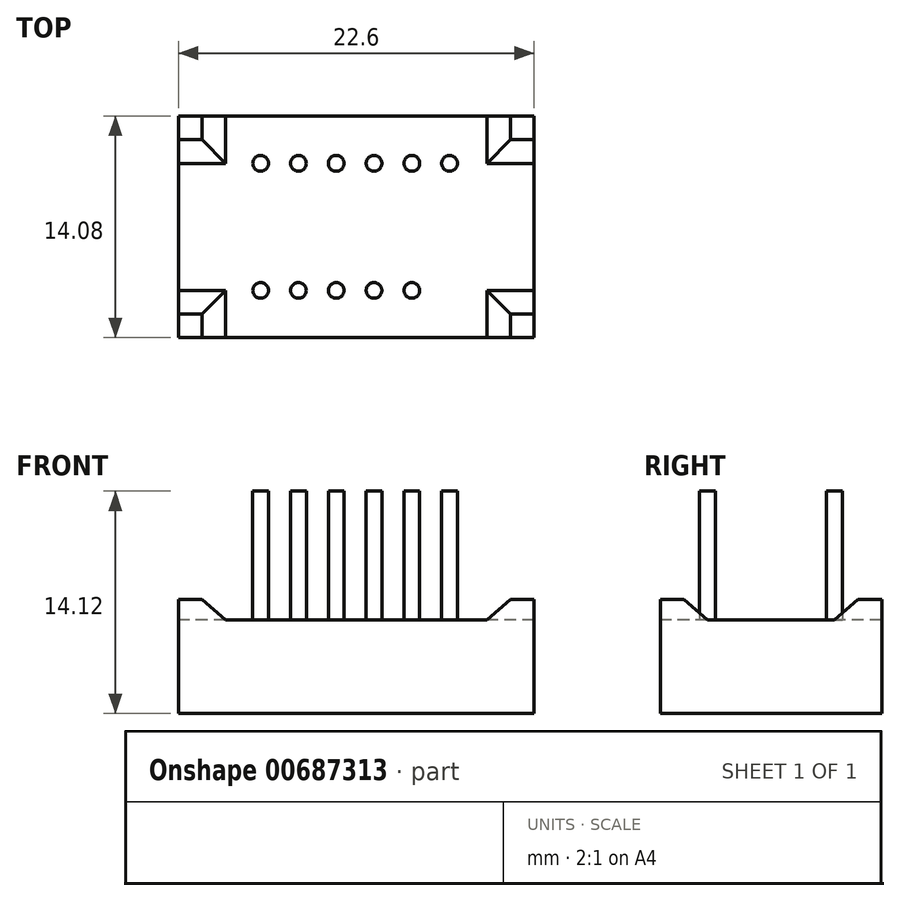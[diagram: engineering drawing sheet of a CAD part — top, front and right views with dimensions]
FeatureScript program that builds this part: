
annotation { "Feature Type Name" : "Feature", "Feature Type Description" : "" }
export const myFeature = defineFeature(function(context is Context, id is Id, definition is map)
    precondition{}
    {
        {
            var Q0;
            Q0=qCreatedBy(makeId("Top.planeOp"),FACE);
            var sketch = newSketch(context, id + "F0", { "sketchPlane" : qUnion([Q0])});
            skLineSegment(sketch, "E0.bottom", {"start": v(11.3, -7.03) * mm, "end": v(-11.3, -7.04) * mm});
            skLineSegment(sketch, "E0.top", {"start": v(11.3, 7.04) * mm, "end": v(-11.3, 7.03) * mm});
            skLineSegment(sketch, "E0.left", {"start": v(11.3, -7.04) * mm, "end": v(11.3, 7.04) * mm});
            skLineSegment(sketch, "E0.right", {"start": v(-11.3, -7.04) * mm, "end": v(-11.3, 7.04) * mm});
            skPoint(sketch, "E0.middle", {"position": v(0, 0) * mm});
            skSolve(sketch);
        }
        {
            var Q0;
            Q0 = qSketchRegion(id + "F0", true);
            extrude(context, id + "F1", {"entities" : qUnion([Q0]), "depth" : 7.24 * mm, "offsetDistance" : 25 * mm});
        }
        {
            var Q0;
            Q0=makeQuery(id+"F1.opExtrude","SWEPT_FACE",FACE,{"disambiguationData":[OSD([sQuery(id+"F0.wireOp",EDGE,"E0.bottom")])]});
            var sketch = newSketch(context, id + "F2", { "sketchPlane" : qUnion([Q0])});
            skLineSegment(sketch, "E1", {"start": v(-9.8, 7.24) * mm, "end": v(-8.3, 5.94) * mm});
            skLineSegment(sketch, "E2", {"start": v(-8.3, 5.94) * mm, "end": v(0, 5.94) * mm});
            skLineSegment(sketch, "E3", {"start": v(-9.8, 7.24) * mm, "end": v(0, 7.24) * mm});
            skLineSegment(sketch, "E4", {"start": v(0, 4.37) * mm, "end": v(0, 9.61) * mm, "construction": true});
            skLineSegment(sketch, "E5.MirrorCS", {"start": v(8.3, 5.94) * mm, "end": v(0, 5.94) * mm});
            skLineSegment(sketch, "E6.MirrorCS", {"start": v(9.8, 7.24) * mm, "end": v(0, 7.24) * mm});
            skLineSegment(sketch, "E7.MirrorCS", {"start": v(9.8, 7.24) * mm, "end": v(8.3, 5.94) * mm});
            skSolve(sketch);
        }
        {
            var Q0;
            Q0 = qSketchRegion(id + "F2", true);
            extrude(context, id + "F3", {"entities" : qUnion([Q0]), "operationType" : NewBodyOperationType.REMOVE, "oppositeDirection" : true, "depth" : 25 * mm, "offsetDistance" : 25 * mm});
        }
        {
            var Q0;
            Q0=makeQuery(id+"F1.opExtrude","SWEPT_FACE",FACE,{"disambiguationData":[OSD([sQuery(id+"F0.wireOp",EDGE,"E0.right")])]});
            var sketch = newSketch(context, id + "F4", { "sketchPlane" : qUnion([Q0])});
            skLineSegment(sketch, "E8", {"start": v(0, 10.08) * mm, "end": v(0, -4.13) * mm, "construction": true});
            skLineSegment(sketch, "E9", {"start": v(-5.54, 7.24) * mm, "end": v(-4.04, 5.94) * mm});
            skLineSegment(sketch, "E10", {"start": v(-4.04, 5.94) * mm, "end": v(0, 5.94) * mm});
            skLineSegment(sketch, "E11", {"start": v(-5.54, 7.24) * mm, "end": v(0, 7.24) * mm});
            skLineSegment(sketch, "E12.MirrorCS", {"start": v(5.54, 7.24) * mm, "end": v(0, 7.24) * mm});
            skLineSegment(sketch, "E13.MirrorCS", {"start": v(4.04, 5.94) * mm, "end": v(0, 5.94) * mm});
            skLineSegment(sketch, "E14.MirrorCS", {"start": v(5.54, 7.24) * mm, "end": v(4.04, 5.94) * mm});
            skSolve(sketch);
        }
        {
            var Q0;
            Q0 = qSketchRegion(id + "F4", true);
            extrude(context, id + "F5", {"entities" : qUnion([Q0]), "operationType" : NewBodyOperationType.REMOVE, "oppositeDirection" : true, "depth" : 25 * mm, "offsetDistance" : 25 * mm});
        }
        {
            var Q0;
            Q0=makeQuery(id+"F5.boolean.opBoolean","MERGE",FACE,{"derivedFrom":[makeQuery(id+"F3.boolean.opBoolean","COPY",FACE,{"derivedFrom":makeQuery(id+"F3.opExtrude","SWEPT_FACE",FACE,{"disambiguationData":[OSD([sQuery(id+"F2.wireOp",EDGE,"E2"),sQuery(id+"F2.wireOp",EDGE,"E5.MirrorCS")])]})})],"fromTools":[makeQuery(id+"F5.opExtrude","SWEPT_FACE",FACE,{"disambiguationData":[OSD([sQuery(id+"F4.wireOp",EDGE,"E10"),sQuery(id+"F4.wireOp",EDGE,"E13.MirrorCS")])]})]});
            var sketch = newSketch(context, id + "F6", { "sketchPlane" : qUnion([Q0])});
            skCircle(sketch, "E15", {"center": v(-6.07, -4.04) * mm, "radius": 0.5 * mm});
            skCircle(sketch, "E16", {"center": v(-6.07, 4.03) * mm, "radius": 0.5 * mm});
            skCircle(sketch, "E17.1.0.0", {"center": v(-3.67, 4.03) * mm, "radius": 0.5 * mm});
            skCircle(sketch, "E17.2.0.0", {"center": v(-1.27, 4.03) * mm, "radius": 0.5 * mm});
            skCircle(sketch, "E17.3.0.0", {"center": v(1.13, 4.03) * mm, "radius": 0.5 * mm});
            skCircle(sketch, "E17.4.0.0", {"center": v(3.53, 4.03) * mm, "radius": 0.5 * mm});
            skCircle(sketch, "E17.5.0.0", {"center": v(5.93, 4.03) * mm, "radius": 0.5 * mm});
            skLineSegment(sketch, "E17.direction1", {"start": v(-6.07, 4.03) * mm, "end": v(-3.67, 4.03) * mm, "construction": true});
            skCircle(sketch, "E18.1.0.0", {"center": v(-3.67, -4.04) * mm, "radius": 0.5 * mm});
            skCircle(sketch, "E18.2.0.0", {"center": v(-1.27, -4.04) * mm, "radius": 0.5 * mm});
            skCircle(sketch, "E18.3.0.0", {"center": v(1.13, -4.04) * mm, "radius": 0.5 * mm});
            skCircle(sketch, "E18.4.0.0", {"center": v(3.53, -4.04) * mm, "radius": 0.5 * mm});
            skLineSegment(sketch, "E18.direction1", {"start": v(-6.07, -4.04) * mm, "end": v(-3.67, -4.04) * mm, "construction": true});
            skSolve(sketch);
        }
        {
            var Q0;
            Q0 = qSketchRegion(id + "F6", true);
            extrude(context, id + "F7", {"entities" : qUnion([Q0]), "operationType" : NewBodyOperationType.ADD, "depth" : 8.18 * mm, "offsetDistance" : 25 * mm});
        }
    });
